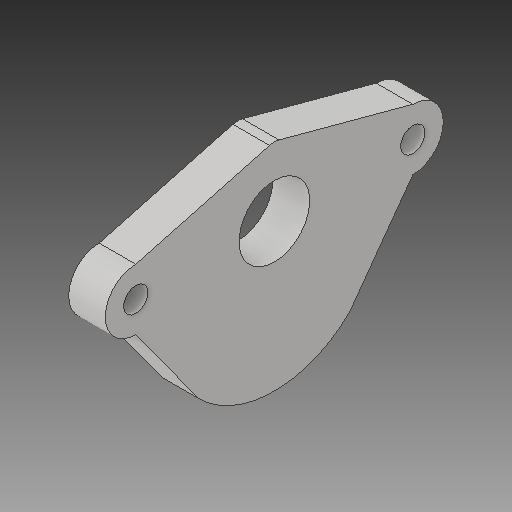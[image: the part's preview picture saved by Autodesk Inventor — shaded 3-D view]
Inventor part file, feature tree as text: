
AUTODESK INVENTOR PART (.ipt)
format: ipt  version: 2017 (Build 210142000, 142)  size: 120,832 bytes
history: native  units: in
note: dims shown in document units (in); Inventor stores cm internally (conversion verified against a paired STEP export)
features: extrude x1, fillet x1
ambient origin geometry x8: Origin, YZ Plane, XZ Plane, XY Plane, X Axis, Y Axis, Z Axis, Center Point
bodies: Solid1 (feature_tree)
feature tree (2):
  extrude  "Extrusion1"  Depth=1.4567in
  fillet  "Fillet1"  Radius=0.166in
